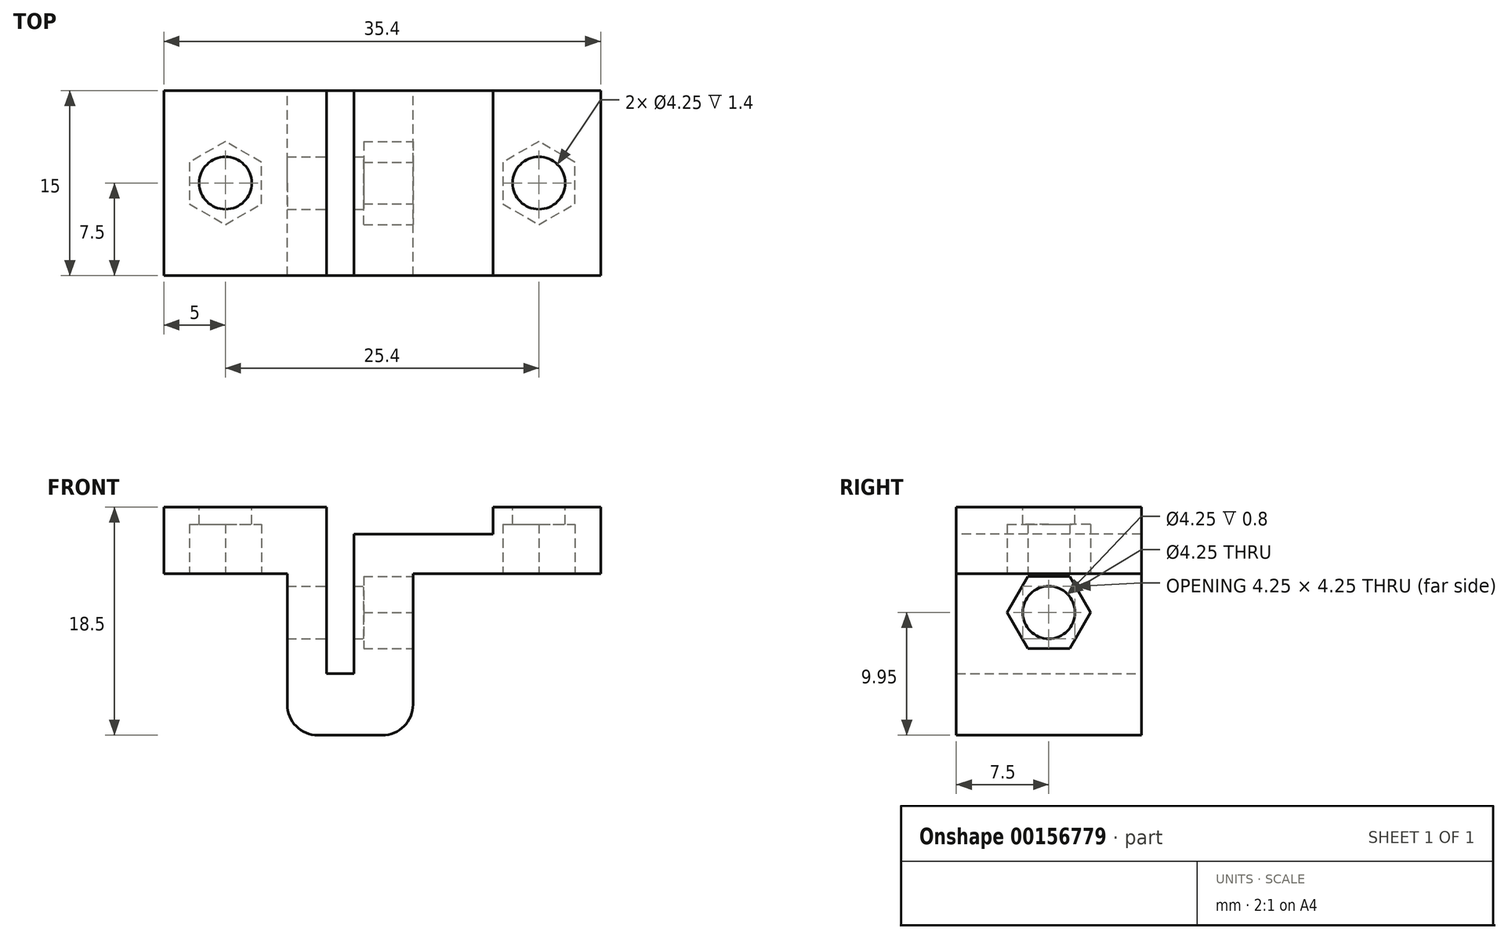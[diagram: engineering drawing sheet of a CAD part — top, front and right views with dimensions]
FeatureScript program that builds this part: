
annotation { "Feature Type Name" : "Feature", "Feature Type Description" : "" }
export const myFeature = defineFeature(function(context is Context, id is Id, definition is map)
    precondition{}
    {
        {
            var Q0;
            Q0=qCreatedBy(makeId("Front.planeOp"),FACE);
            var sketch = newSketch(context, id + "F0", { "sketchPlane" : qUnion([Q0])});
            skLineSegment(sketch, "E0", {"start": v(-15.4, 0) * mm, "end": v(-2.2, 0) * mm});
            skLineSegment(sketch, "E1", {"start": v(20, 0) * mm, "end": v(20, -3.2) * mm});
            skLineSegment(sketch, "E2", {"start": v(20, -3.2) * mm, "end": v(4.8, -3.2) * mm});
            skLineSegment(sketch, "E3", {"start": v(4.8, -3.2) * mm, "end": v(4.8, -13.8) * mm});
            skLineSegment(sketch, "E4", {"start": v(2.3, -16.3) * mm, "end": v(-2.9, -16.3) * mm});
            skLineSegment(sketch, "E5", {"start": v(-5.4, -13.8) * mm, "end": v(-5.4, -3.2) * mm});
            skLineSegment(sketch, "E6", {"start": v(-5.4, -3.2) * mm, "end": v(-15.4, -3.2) * mm});
            skLineSegment(sketch, "E7", {"start": v(-15.4, -3.2) * mm, "end": v(-15.4, 0) * mm});
            skLineSegment(sketch, "E8", {"start": v(-2.2, 0) * mm, "end": v(-2.2, -11.3) * mm});
            skLineSegment(sketch, "E9", {"start": v(-2.2, -11.3) * mm, "end": v(0, -11.3) * mm});
            skLineSegment(sketch, "E10", {"start": v(0, -11.3) * mm, "end": v(0, 0) * mm});
            skPoint(sketch, "E11.visualSharp", {"position": v(-5.4, -16.3) * mm});
            skArc(sketch, "E11.filletArc", {"start": v(-5.4, -13.8) * mm, "mid": v(-4.67, -15.57) * mm, "end": v(-2.9, -16.3) * mm});
            skPoint(sketch, "E12.visualSharp", {"position": v(4.8, -16.3) * mm});
            skArc(sketch, "E12.filletArc", {"start": v(2.3, -16.3) * mm, "mid": v(4.07, -15.57) * mm, "end": v(4.8, -13.8) * mm});
            skLineSegment(sketch, "E13.trimOffspring", {"start": v(0, 0) * mm, "end": v(20, 0) * mm});
            skSolve(sketch);
        }
        {
            var Q0;
            Q0=qSketchRegion(id+"F0",true);
            extrude(context, id + "F1", {"entities" : qUnion([Q0]), "endBound" : BoundingType.SYMMETRIC, "depth" : 15 * mm});
        }
        {
            var Q0;
            Q0=makeQuery(id+"F1.opExtrude","SWEPT_FACE",FACE,{"disambiguationData":[OSD([sQuery(id+"F0.wireOp",EDGE,"E13.trimOffspring")])]});
            var sketch = newSketch(context, id + "F2", { "sketchPlane" : qUnion([Q0])});
            skLineSegment(sketch, "E14.bottom", {"start": v(20, 7.5) * mm, "end": v(11.3, 7.5) * mm});
            skLineSegment(sketch, "E14.top", {"start": v(20, -7.5) * mm, "end": v(11.3, -7.5) * mm});
            skLineSegment(sketch, "E14.left", {"start": v(20, 7.5) * mm, "end": v(20, -7.5) * mm});
            skLineSegment(sketch, "E14.right", {"start": v(11.3, 7.5) * mm, "end": v(11.3, -7.5) * mm});
            skLineSegment(sketch, "E15.bottom", {"start": v(-15.4, 7.5) * mm, "end": v(-2.2, 7.5) * mm});
            skLineSegment(sketch, "E15.top", {"start": v(-15.4, -7.5) * mm, "end": v(-2.2, -7.5) * mm});
            skLineSegment(sketch, "E15.left", {"start": v(-15.4, 7.5) * mm, "end": v(-15.4, -7.5) * mm});
            skLineSegment(sketch, "E15.right", {"start": v(-2.2, 7.5) * mm, "end": v(-2.2, -7.5) * mm});
            skSolve(sketch);
        }
        {
            var Q0;
            Q0 = qSketchRegion(id + "F2", true);
            extrude(context, id + "F3", {"entities" : qUnion([Q0]), "operationType" : NewBodyOperationType.ADD, "depth" : 2.2 * mm});
        }
        {
            var Q0;
            Q0=makeQuery(id+"F3.opExtrude","CAP_FACE",FACE,{"disambiguationData":[OSD([sQuery(id+"F2.wireOp",EDGE,"E15.bottom"),sQuery(id+"F2.wireOp",EDGE,"E15.top"),sQuery(id+"F2.wireOp",EDGE,"E15.left"),sQuery(id+"F2.wireOp",EDGE,"E15.right")])],"isStart":false});
            var sketch = newSketch(context, id + "F4", { "sketchPlane" : qUnion([Q0])});
            skCircle(sketch, "E16", {"center": v(-10.4, 0) * mm, "radius": 2.12 * mm});
            skCircle(sketch, "E17", {"center": v(15, 0) * mm, "radius": 2.12 * mm});
            skSolve(sketch);
        }
        {
            var Q0;
            Q0 = qSketchRegion(id + "F4", true);
            extrude(context, id + "F5", {"entities" : qUnion([Q0]), "operationType" : NewBodyOperationType.REMOVE, "oppositeDirection" : true, "depth" : 25 * mm});
        }
        {
            var Q0;
            Q0=makeQuery(id+"F1.opExtrude","SWEPT_FACE",FACE,{"disambiguationData":[OSD([sQuery(id+"F0.wireOp",EDGE,"E6")])]});
            var sketch = newSketch(context, id + "F6", { "sketchPlane" : qUnion([Q0])});
            skCircle(sketch, "E18.cCircle", {"center": v(-10.4, 0) * mm, "radius": 2.93 * mm, "construction": true});
            skLineSegment(sketch, "E18.0", {"start": v(-7.48, 1.69) * mm, "end": v(-7.48, -1.69) * mm});
            skLineSegment(sketch, "E18.1", {"start": v(-7.48, -1.69) * mm, "end": v(-10.4, -3.38) * mm});
            skLineSegment(sketch, "E18.2", {"start": v(-10.4, -3.38) * mm, "end": v(-13.33, -1.69) * mm});
            skLineSegment(sketch, "E18.3", {"start": v(-13.33, -1.69) * mm, "end": v(-13.33, 1.69) * mm});
            skLineSegment(sketch, "E18.4", {"start": v(-13.33, 1.69) * mm, "end": v(-10.4, 3.38) * mm});
            skLineSegment(sketch, "E18.5", {"start": v(-10.4, 3.38) * mm, "end": v(-7.48, 1.69) * mm});
            skPoint(sketch, "E18.0.midPoint", {"position": v(-7.48, 0) * mm});
            skCircle(sketch, "E19.cCircle", {"center": v(15, 0) * mm, "radius": 2.93 * mm, "construction": true});
            skPoint(sketch, "E19.cCircle.centerSnap0", {"position": v(-5.4, 0) * mm});
            skPoint(sketch, "E19.cCircle.perimeterSnap0", {"position": v(-5.4, 0) * mm});
            skLineSegment(sketch, "E19.0", {"start": v(17.92, 1.69) * mm, "end": v(17.92, -1.69) * mm});
            skLineSegment(sketch, "E19.1", {"start": v(17.92, -1.69) * mm, "end": v(15, -3.38) * mm});
            skLineSegment(sketch, "E19.2", {"start": v(15, -3.38) * mm, "end": v(12.07, -1.69) * mm});
            skLineSegment(sketch, "E19.3", {"start": v(12.07, -1.69) * mm, "end": v(12.07, 1.69) * mm});
            skLineSegment(sketch, "E19.4", {"start": v(12.07, 1.69) * mm, "end": v(15, 3.38) * mm});
            skLineSegment(sketch, "E19.5", {"start": v(15, 3.38) * mm, "end": v(17.92, 1.69) * mm});
            skPoint(sketch, "E19.0.midPoint", {"position": v(17.92, 0) * mm});
            skPoint(sketch, "E19.0.midPoint.positionSnap0", {"position": v(-5.4, 0) * mm});
            skSolve(sketch);
        }
        {
            var Q0;
            Q0 = qSketchRegion(id + "F6", true);
            extrude(context, id + "F7", {"entities" : qUnion([Q0]), "operationType" : NewBodyOperationType.REMOVE, "oppositeDirection" : true, "depth" : 4 * mm});
        }
        {
            var Q0;
            Q0=makeQuery(id+"F1.opExtrude","SWEPT_FACE",FACE,{"disambiguationData":[OSD([sQuery(id+"F0.wireOp",EDGE,"E3")])]});
            var sketch = newSketch(context, id + "F8", { "sketchPlane" : qUnion([Q0])});
            skCircle(sketch, "E20", {"center": v(0, -6.35) * mm, "radius": 2.12 * mm});
            skSolve(sketch);
        }
        {
            var Q0;
            Q0 = qSketchRegion(id + "F8", true);
            extrude(context, id + "F9", {"entities" : qUnion([Q0]), "operationType" : NewBodyOperationType.REMOVE, "oppositeDirection" : true, "depth" : 25 * mm});
        }
        {
            var Q0;
            Q0=makeQuery(id+"F1.opExtrude","SWEPT_FACE",FACE,{"disambiguationData":[OSD([sQuery(id+"F0.wireOp",EDGE,"E3")])]});
            var sketch = newSketch(context, id + "F10", { "sketchPlane" : qUnion([Q0])});
            skCircle(sketch, "E21.cCircle", {"center": v(0, -6.35) * mm, "radius": 2.93 * mm, "construction": true});
            skLineSegment(sketch, "E21.0", {"start": v(1.69, -9.27) * mm, "end": v(-1.69, -9.27) * mm});
            skLineSegment(sketch, "E21.1", {"start": v(-1.69, -9.27) * mm, "end": v(-3.38, -6.35) * mm});
            skLineSegment(sketch, "E21.2", {"start": v(-3.38, -6.35) * mm, "end": v(-1.69, -3.43) * mm});
            skLineSegment(sketch, "E21.3", {"start": v(-1.69, -3.43) * mm, "end": v(1.69, -3.42) * mm});
            skLineSegment(sketch, "E21.4", {"start": v(1.69, -3.42) * mm, "end": v(3.38, -6.35) * mm});
            skLineSegment(sketch, "E21.5", {"start": v(3.38, -6.35) * mm, "end": v(1.69, -9.27) * mm});
            skPoint(sketch, "E21.0.midPoint", {"position": v(0, -9.27) * mm});
            skSolve(sketch);
        }
        {
            var Q0;
            Q0 = qSketchRegion(id + "F10", true);
            extrude(context, id + "F11", {"entities" : qUnion([Q0]), "operationType" : NewBodyOperationType.REMOVE, "oppositeDirection" : true, "depth" : 4 * mm});
        }
    });
